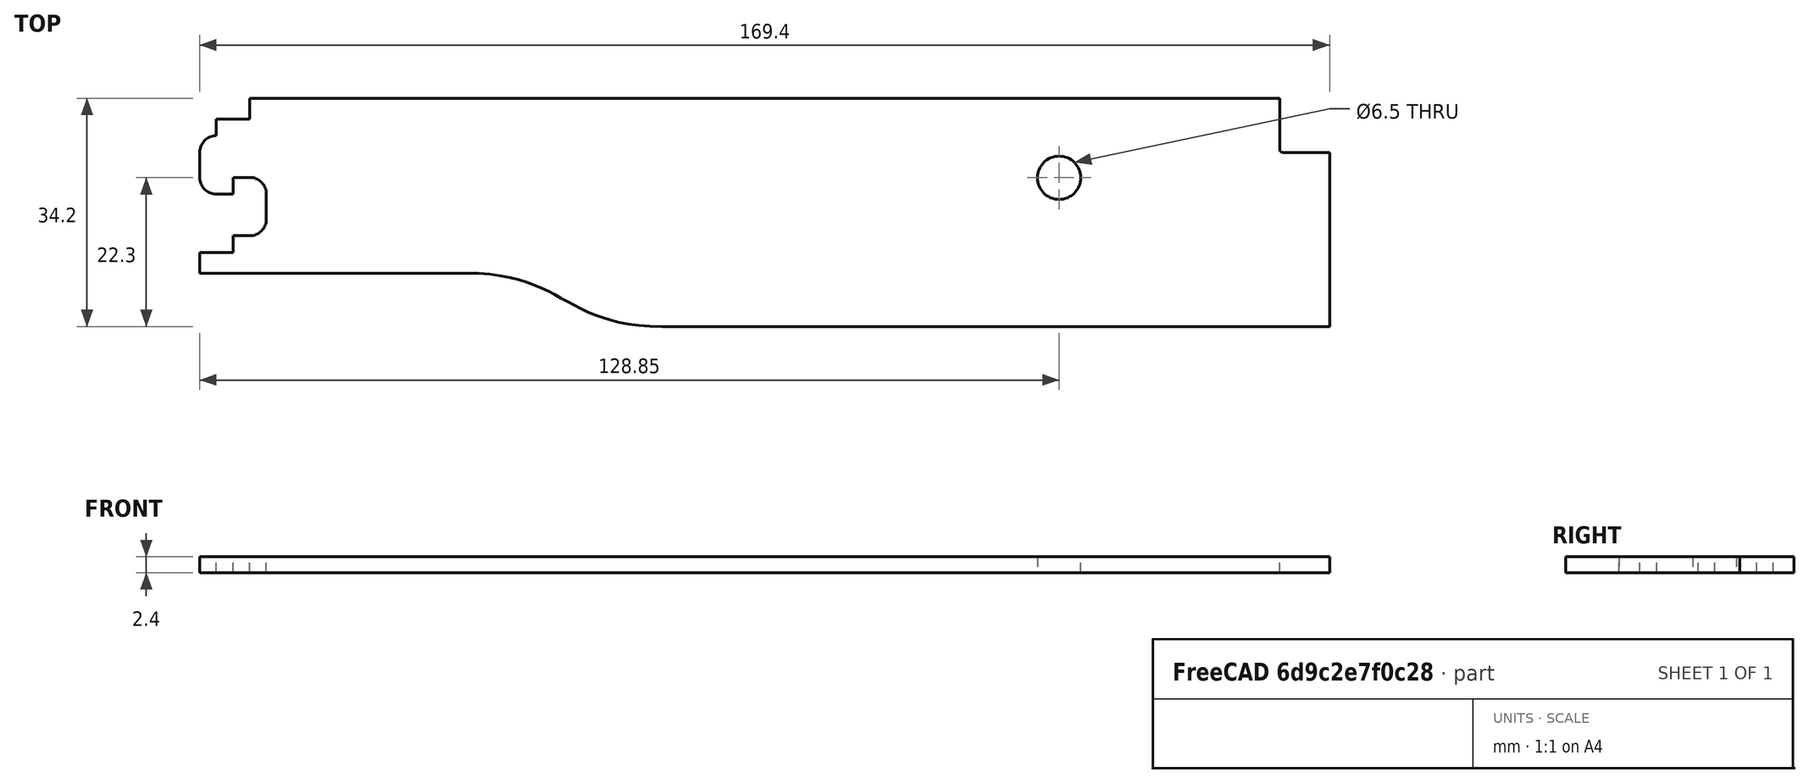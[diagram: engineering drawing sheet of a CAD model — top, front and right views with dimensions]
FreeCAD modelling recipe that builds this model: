
FCSTD DOCUMENT  (FreeCAD 0.19R0.19.2)
Label: v0_27
License: All rights reserved
LicenseURL: http://en.wikipedia.org/wiki/All_rights_reserved
objects: Sketcher::SketchObject×2, Part::Extrusion×1
note: 3 computed .brp shape members not serialized (recipe doc carries the construction recipe); baked Part::Feature solids carry a one-line shape summary decoded from their .brp

FEATURE [Sketcher::SketchObject] Sketch
  FullyConstrained = true
  sketch-geometry (33):
    g0: LineSegment StartX=0 StartY=0 StartZ=0 EndX=154.4 EndY=0 EndZ=0
    g1: Circle CenterX=121.35 CenterY=-11.9 CenterZ=0 NormalX=0 NormalY=0 NormalZ=1 AngleXU=0 Radius=3.25
    g2: LineSegment StartX=154.4 StartY=0 StartZ=0 EndX=154.4 EndY=-7.6 EndZ=0
    g3: ArcOfCircle CenterX=154.9 CenterY=-7.6 CenterZ=0 NormalX=0 NormalY=0 NormalZ=1 AngleXU=0 Radius=0.5 StartAngle=3.14159 EndAngle=4.71239
    g4: LineSegment StartX=-5 StartY=-3.1 StartZ=0 EndX=0 EndY=-3.1 EndZ=0
    g5: LineSegment StartX=-5 StartY=-3.1 StartZ=0 EndX=-5 EndY=-5.6 EndZ=0
    g6: LineSegment StartX=-7.5 StartY=-8.1 StartZ=0 EndX=-7.5 EndY=-11.85 EndZ=0
    g7: ArcOfCircle CenterX=-5 CenterY=-8.1 CenterZ=0 NormalX=0 NormalY=0 NormalZ=1 AngleXU=0 Radius=2.5 StartAngle=1.5708 EndAngle=3.14159
    g8: LineSegment StartX=-5 StartY=-14.35 StartZ=0 EndX=-2.5 EndY=-14.35 EndZ=0
    g9: ArcOfCircle CenterX=-5 CenterY=-11.85 CenterZ=0 NormalX=0 NormalY=0 NormalZ=1 AngleXU=0 Radius=2.5 StartAngle=3.14159 EndAngle=4.71239
    g10: LineSegment StartX=-2.5 StartY=-14.35 StartZ=0 EndX=-2.5 EndY=-11.85 EndZ=0
    g11: LineSegment StartX=-2.5 StartY=-11.85 StartZ=0 EndX=1.492e-13 EndY=-11.85 EndZ=0
    g12: ArcOfCircle CenterX=1.492e-13 CenterY=-14.35 CenterZ=0 NormalX=0 NormalY=0 NormalZ=1 AngleXU=0 Radius=2.5 StartAngle=8e-16 EndAngle=1.5708
    g13: LineSegment StartX=2.5 StartY=-14.35 StartZ=0 EndX=2.5 EndY=-18.1 EndZ=0
    g14: ArcOfCircle CenterX=1.474e-13 CenterY=-18.1 CenterZ=0 NormalX=0 NormalY=0 NormalZ=1 AngleXU=0 Radius=2.5 StartAngle=4.71239 EndAngle=6.28319
    g15: LineSegment StartX=-2.5 StartY=-20.6 StartZ=0 EndX=1.47e-13 EndY=-20.6 EndZ=0
    g16: LineSegment StartX=-2.5 StartY=-20.6 StartZ=0 EndX=-2.5 EndY=-23.1 EndZ=0
    g17: LineSegment StartX=-7.5 StartY=-23.1 StartZ=0 EndX=-2.5 EndY=-23.1 EndZ=0
    g18: LineSegment StartX=32.5209 StartY=-26.2 StartZ=0 EndX=-7.5 EndY=-26.2 EndZ=0
    g19: LineSegment StartX=61.85 StartY=-34.2 StartZ=0 EndX=161.9 EndY=-34.2 EndZ=0
    g20: LineSegment StartX=161.9 StartY=-8.1 StartZ=0 EndX=161.9 EndY=-34.2 EndZ=0
    g21: LineSegment StartX=154.9 StartY=-8.1 StartZ=0 EndX=161.9 EndY=-8.1 EndZ=0
    g22: LineSegment StartX=-7.5 StartY=-23.1 StartZ=0 EndX=-7.5 EndY=-26.2 EndZ=0
    g23: LineSegment StartX=0 StartY=0 StartZ=0 EndX=0 EndY=-3.1 EndZ=0
    g24-g28: Circle x5 (B-spline internal-alignment scaffolding for g29; pole/knot coordinates omitted)
    g29: BSplineCurve PolesCount=5 KnotsCount=3 Degree=3 IsPeriodic=0
    g30: GeomPoint X=61.85 Y=-34.2 Z=0
    g31: GeomPoint X=47.185 Y=-30.2 Z=0
    g32: GeomPoint X=32.5209 Y=-26.2 Z=0
  constraints (67):
    c: PointOnObject(g0,g-2)
    c: Horizontal(g0)
    c: Distance(g0) = 154.4
    c: DistanceY(g-1,g0) = 0
    c: Block(g1)
    c: Vertical(g2)
    c: Distance(g2) = 7.6
    c: Coincident(g2,g0)
    c: Block(g3)
    c: Horizontal(g4)
    c: Vertical(g5)
    c: Coincident(g5,g4)
    c: Vertical(g6)
    c: Coincident(g7,g5)
    c: Block(g7)
    c: Coincident(g6,g7)
    c: Horizontal(g8)
    c: Coincident(g9,g6)
    c: Block(g9)
    c: Block(g8)
    c: Vertical(g10)
    c: Coincident(g10,g8)
    c: Horizontal(g11)
    c: Coincident(g11,g10)
    c: Coincident(g12,g11)
    c: Vertical(g13)
    c: Block(g12)
    c: Coincident(g13,g12)
    c: Coincident(g14,g13)
    c: Block(g14)
    c: Horizontal(g15)
    c: Coincident(g15,g14)
    c: Vertical(g16)
    c: Coincident(g16,g15)
    c: Horizontal(g17)
    c: Coincident(g17,g16)
    c: Block(g16)
    c: Block(g4)
    c: Horizontal(g19)
    c: Horizontal(g18)
    c: Block(g18)
    c: Block(g19)
    c: Vertical(g20)
    c: Distance(g20) = 26.1
    c: Coincident(g20,g19)
    c: Horizontal(g21)
    c: Coincident(g21,g20)
    c: Coincident(g21,g3)
    c: Distance(g21) = 7
    c: Distance(g16) = 2.5
    c: Distance(g16) = 2.5
    c: Block(g17)
    c: Vertical(g22)
    c: Coincident(g22,g17)
    c: Coincident(g22,g18)
    c: Vertical(g23)
    c: Coincident(g23,g0)
    c: Coincident(g23,g4)
    c: Coincident(g29,g19)
    c: Weight(g24) = 1
    c: Equal(g24, g25-g28) x4
    c: Coincident(g29,g18)
    c: InternalAlignment(g24-g28 -> g29) x5
    c: InternalAlignment(g30,g29)
    c: InternalAlignment(g31,g29)
    c: InternalAlignment(g32,g29)
    c: Block(g29)
FEATURE [Part::Extrusion] Extrude
  Base = -> Sketch
  Dir = (0,0,1)
  DirMode = 2
  FaceMakerClass = Part::FaceMakerBullseye
  LengthFwd = 2.4
  LengthRev = 0
  Solid = true
  Symmetric = false
FEATURE [Sketcher::SketchObject] Sketch001
  FullyConstrained = false
  sketch-geometry (61):
    g0: ArcOfCircle CenterX=144.4 CenterY=-10 CenterZ=0 NormalX=0 NormalY=0 NormalZ=1 AngleXU=0 Radius=5 StartAngle=0 EndAngle=1.5708
    g1: LineSegment StartX=20 StartY=-23 StartZ=0 EndX=54.35 EndY=-23 EndZ=0
    g2: ArcOfCircle CenterX=20 CenterY=-18 CenterZ=0 NormalX=0 NormalY=0 NormalZ=1 AngleXU=0 Radius=5 StartAngle=3.14159 EndAngle=4.71239
    g3: ArcOfCircle CenterX=20 CenterY=-10 CenterZ=0 NormalX=0 NormalY=0 NormalZ=1 AngleXU=0 Radius=5 StartAngle=1.5708 EndAngle=3.14159
    g4: LineSegment StartX=15 StartY=-10 StartZ=0 EndX=15 EndY=-18 EndZ=0
    g5: LineSegment StartX=32.5209 StartY=-26.2 StartZ=0 EndX=-7.49911 EndY=-26.2 EndZ=0
    g6: LineSegment StartX=61.85 StartY=-34.2 StartZ=0 EndX=161.9 EndY=-34.2 EndZ=0
    g7: LineSegment StartX=161.9 StartY=-34.2 StartZ=0 EndX=161.9 EndY=-8.1 EndZ=0
    g8: ArcOfCircle CenterX=144.4 CenterY=-24.1 CenterZ=0 NormalX=0 NormalY=0 NormalZ=1 AngleXU=0 Radius=5 StartAngle=4.71239 EndAngle=6.28319
    g9: LineSegment StartX=104.85 StartY=-29.1 StartZ=0 EndX=144.4 EndY=-29.1 EndZ=0
    g10: LineSegment StartX=-5 StartY=-3.1 StartZ=0 EndX=0 EndY=-3.1 EndZ=0
    g11: LineSegment StartX=-5 StartY=-3.1 StartZ=0 EndX=-5 EndY=-5.6 EndZ=0
    g12: LineSegment StartX=-7.49911 StartY=-8.1 StartZ=0 EndX=-7.49911 EndY=-11.85 EndZ=0
    g13: ArcOfCircle CenterX=-4.99911 CenterY=-8.1 CenterZ=0 NormalX=0 NormalY=0 NormalZ=1 AngleXU=0 Radius=2.5 StartAngle=1.57115 EndAngle=3.14159
    g14: LineSegment StartX=-4.99911 StartY=-14.35 StartZ=0 EndX=-2.49911 EndY=-14.35 EndZ=0
    g15: ArcOfCircle CenterX=-4.99911 CenterY=-11.85 CenterZ=0 NormalX=0 NormalY=0 NormalZ=1 AngleXU=0 Radius=2.5 StartAngle=3.14159 EndAngle=4.71239
    g16: LineSegment StartX=-2.49911 StartY=-14.35 StartZ=0 EndX=-2.49911 EndY=-11.85 EndZ=0
    g17: LineSegment StartX=-2.49911 StartY=-11.85 StartZ=0 EndX=0.000891 EndY=-11.85 EndZ=0
    g18: ArcOfCircle CenterX=0.000891 CenterY=-14.35 CenterZ=0 NormalX=0 NormalY=0 NormalZ=1 AngleXU=0 Radius=2.5 StartAngle=8e-16 EndAngle=1.5708
    g19: LineSegment StartX=2.50089 StartY=-14.35 StartZ=0 EndX=2.50089 EndY=-18.1 EndZ=0
    g20: ArcOfCircle CenterX=0.000891 CenterY=-18.1 CenterZ=0 NormalX=0 NormalY=0 NormalZ=1 AngleXU=0 Radius=2.5 StartAngle=4.71239 EndAngle=6.28319
    g21: LineSegment StartX=-2.49911 StartY=-20.6 StartZ=0 EndX=0.000891 EndY=-20.6 EndZ=0
    g22: LineSegment StartX=-2.49911 StartY=-20.6 StartZ=0 EndX=-2.49911 EndY=-23.1 EndZ=0
    g23: LineSegment StartX=-7.49911 StartY=-23.1 StartZ=0 EndX=-2.49911 EndY=-23.1 EndZ=0
    g24: LineSegment StartX=20 StartY=-5 StartZ=0 EndX=54.35 EndY=-5 EndZ=0
    g25: LineSegment StartX=60.35 StartY=-32.2 StartZ=0 EndX=98.85 EndY=-32.2 EndZ=0
    g26: LineSegment StartX=104.85 StartY=-29.1 StartZ=0 EndX=104.85 EndY=-29.2 EndZ=0
    g27: LineSegment StartX=54.35 StartY=-23 StartZ=0 EndX=54.35 EndY=-29.2 EndZ=0
    g28: Circle CenterX=104.85 CenterY=-29.2 CenterZ=0 NormalX=0 NormalY=0 NormalZ=1 AngleXU=0 Radius=1
    g29: Circle CenterX=104.85 CenterY=-32.2 CenterZ=0 NormalX=0 NormalY=0 NormalZ=1 AngleXU=0 Radius=1
    g30: Circle CenterX=98.85 CenterY=-32.2 CenterZ=0 NormalX=0 NormalY=0 NormalZ=1 AngleXU=0 Radius=1
    g31: BSplineCurve PolesCount=3 KnotsCount=2 Degree=2 IsPeriodic=0
    g32: GeomPoint X=104.85 Y=-29.2 Z=0
    g33: GeomPoint X=98.85 Y=-32.2 Z=0
    g34: Circle CenterX=54.35 CenterY=-29.2 CenterZ=0 NormalX=0 NormalY=0 NormalZ=1 AngleXU=0 Radius=1
    g35: Circle CenterX=60.35 CenterY=-32.2 CenterZ=0 NormalX=0 NormalY=0 NormalZ=1 AngleXU=0 Radius=1
    g36: BSplineCurve PolesCount=3 KnotsCount=2 Degree=2 IsPeriodic=0
    g37: GeomPoint X=54.35 Y=-29.2 Z=0
    g38: GeomPoint X=60.35 Y=-32.2 Z=0
    g39: LineSegment StartX=104.85 StartY=-5 StartZ=0 EndX=144.4 EndY=-5 EndZ=0
    g40: LineSegment StartX=54.35 StartY=-5 StartZ=0 EndX=54.35 EndY=-4.1 EndZ=0
    g41: ArcOfCircle CenterX=56.35 CenterY=-4.1 CenterZ=0 NormalX=0 NormalY=0 NormalZ=1 AngleXU=0 Radius=2 StartAngle=1.5708 EndAngle=3.14159
    g42: LineSegment StartX=104.85 StartY=-5 StartZ=0 EndX=104.85 EndY=-4.1 EndZ=0
    g43: ArcOfCircle CenterX=102.85 CenterY=-4.1 CenterZ=0 NormalX=0 NormalY=0 NormalZ=1 AngleXU=0 Radius=2 StartAngle=1e-16 EndAngle=1.5708
    g44: LineSegment StartX=56.35 StartY=-2.1 StartZ=0 EndX=102.85 EndY=-2.1 EndZ=0
    g45: LineSegment StartX=0 StartY=0 StartZ=0 EndX=154.4 EndY=0 EndZ=0
    g46: LineSegment StartX=149.4 StartY=-10 StartZ=0 EndX=149.4 EndY=-24.1 EndZ=0
    g47: ArcOfCircle CenterX=154.9 CenterY=-7.6 CenterZ=0 NormalX=0 NormalY=0 NormalZ=1 AngleXU=0 Radius=0.5 StartAngle=3.14159 EndAngle=4.71239
    g48-g52: Circle x5 (B-spline internal-alignment scaffolding for g53; pole/knot coordinates omitted)
    g53: BSplineCurve PolesCount=5 KnotsCount=3 Degree=3 IsPeriodic=0
    g54: GeomPoint X=61.85 Y=-34.2 Z=0
    g55: GeomPoint X=47.1857 Y=-30.2 Z=0
    g56: GeomPoint X=32.5209 Y=-26.2 Z=0
    g57: LineSegment StartX=-7.49911 StartY=-23.1 StartZ=0 EndX=-7.49911 EndY=-26.2 EndZ=0
    g58: LineSegment StartX=0 StartY=0 StartZ=0 EndX=0 EndY=-3.1 EndZ=0
    g59: LineSegment StartX=154.4 StartY=0 StartZ=0 EndX=154.4 EndY=-7.6 EndZ=0
    g60: LineSegment StartX=155.605 StartY=-8.1 StartZ=0 EndX=161.9 EndY=-8.1 EndZ=0
  constraints (127):
    c: PointOnObject(g45,g-2)
    c: DistanceY(g-1,g45) = 0
    c: Block(g0)
    c: Horizontal(g1)
    c: Block(g2)
    c: Block(g1)
    c: Block(g3)
    c: Coincident(g4,g3)
    c: Coincident(g4,g2)
    c: Horizontal(g6)
    c: Horizontal(g5)
    c: Vertical(g7)
    c: Coincident(g7,g6)
    c: Block(g8)
    c: Horizontal(g9)
    c: Coincident(g9,g8)
    c: Block(g9)
    c: Distance(g5) = 40.02
    c: Horizontal(g10)
    c: Vertical(g11)
    c: Coincident(g11,g10)
    c: Vertical(g12)
    c: Coincident(g13,g11)
    c: Block(g13)
    c: Horizontal(g14)
    c: Block(g15)
    c: Block(g14)
    c: Vertical(g16)
    c: Coincident(g16,g14)
    c: Horizontal(g17)
    c: Coincident(g17,g16)
    c: Coincident(g18,g17)
    c: Vertical(g19)
    c: Block(g18)
    c: Block(g20)
    c: Horizontal(g21)
    c: Coincident(g21,g20)
    c: Vertical(g22)
    c: Coincident(g22,g21)
    c: Coincident(g23,g22)
    c: Equal(g10,g23)
    c: Equal(g22,g11)
    c: Block(g21)
    c: Block(g12)
    c: Block(g19)
    c: Block(g23)
    c: Block(g22)
    c: Horizontal(g24)
    c: Coincident(g24,g3)
    c: Horizontal(g25)
    c: Distance(g25) = 38.5
    c: Vertical(g26)
    c: Distance(g26) = 0.1
    c: Coincident(g26,g9)
    c: Vertical(g27)
    c: Distance(g27) = 6.2
    c: Coincident(g27,g1)
    c: Coincident(g31,g26)
    c: Weight(g28) = 1
    c: Equal(g28,g29)
    c: Equal(g28,g30)
    c: Coincident(g31,g25)
    c: InternalAlignment(g28,g31)
    c: InternalAlignment(g29,g31)
    c: InternalAlignment(g30,g31)
    c: InternalAlignment(g32,g31)
    c: InternalAlignment(g33,g31)
    c: Block(g31)
    c: Block(g25)
    c: Weight(g34) = 1
    c: Equal(g34,g35)
    c: Coincident(g36,g25)
    c: InternalAlignment(g34,g36)
    c: InternalAlignment(g35,g36)
    c: InternalAlignment(g37,g36)
    c: InternalAlignment(g38,g36)
    c: Block(g36)
    c: Coincident(g39,g0)
    c: Distance(g39) = 39.55
    c: Vertical(g40)
    c: Distance(g40) = 0.9
    c: Distance(g24) = 34.35
    c: Block(g24)
    c: Block(g41)
    c: Block(g40)
    c: Vertical(g42)
    c: Block(g39)
    c: Distance(g42) = 0.9
    c: Coincident(g43,g42)
    c: Block(g43)
    c: Block(g42)
    c: Horizontal(g44)
    c: Coincident(g44,g41)
    c: Coincident(g44,g43)
    c: Horizontal(g45)
    c: Vertical(g46)
    c: Coincident(g46,g0)
    c: Coincident(g46,g8)
    c: Block(g46)
    c: Block(g6)
    c: Block(g45)
    c: Block(g47)
    c: Block(g7)
    c: Coincident(g53,g6)
    c: Weight(g48) = 1
    c: Equal(g48, g49-g52) x4
    c: Coincident(g53,g5)
    c: InternalAlignment(g48-g52 -> g53) x5
    c: InternalAlignment(g54,g53)
    c: InternalAlignment(g55,g53)
    c: InternalAlignment(g56,g53)
    c: Block(g53)
    c: Vertical(g57)
    c: Coincident(g57,g23)
    c: Coincident(g57,g5)
    c: Block(g57)
    c: Vertical(g58)
    c: Coincident(g58,g45)
    c: Coincident(g58,g10)
    c: Distance(g58) = 3.1
    c: Vertical(g59)
    c: Coincident(g59,g45)
    c: Coincident(g47,g59)
    c: Distance(g59) = 7.6
    c: Horizontal(g60)
    c: Coincident(g60,g7)
    c: Block(g59)
